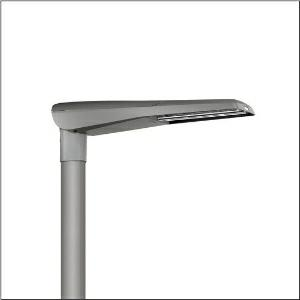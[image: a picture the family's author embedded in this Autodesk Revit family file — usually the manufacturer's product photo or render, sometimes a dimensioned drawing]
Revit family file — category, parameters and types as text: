
# Revit family: streetlight_sl_11_iq_mini___pc-l_5xc2ec1f08he_97a8
name_source: partatom
category: Lighting Fixtures
units: mm (PartAtom-declared; Revit-internal decimal feet)

## family parameters
Cut with Voids When Loaded = No
Host = Face
Light Source = No
Part Type = Normal
Room Calculation Point = No
Round Connector Dimension = Use Diameter
Shared = No

## types (1)
- --- (1 x LED, 5820 lm, 63.6 W, 2200K)
    Apparent Load = 64 VA
    CIE Flux Codes = 37 73 96 100 100
    Color Rendering = 70
    Color Temperature = 2200K
    Default Elevation = 1800 mm
    Description = Streetlight SL 11 iQ mini, mast luminaire, primary light control with 3 zone facetted reflector, of plastic, silver coated, highly specular, primary optical cover: cover, of PMMA, transparent, light distribution: PC-L, light emission: direct distribution, primary light characteristic: asymmetric, left, installation type: post-top, side-entry, lamps: LED, High Power LED, rated values: 7.110lm | 62,2W | 114,3lm/W (begin service life); end service life: 7.110lm | 65,6W; at 50% lumin. flux: 3.555lm | 29,4W | 120,9lm/W, colour temperature: 2200/2700/3000/4000K, colour rendering: CRI > 70, light colour: 722/727/730/740, light setting 1 begin service life: 100% | 7.110lm | 62,2W | 114,3lm/W | 3.000K, light setting 1 end service life: 65,6W, further light settings possible, control: Street-Remote, Auto-Match, Temp-Guard, Lumen-Switch, Night-Set, Smart-Wire, Light-Fading, Desk-Remote (wireless, voltage-free reading and setting of iQ features in the workshop via application-optimized NFC function/RFID function), optimised constant luminous flux control (CLO 2.0), with cable H07RN-F 5x 1.5mm², mains connection: 230..240V, AC, 50/60Hz, connection cable pre-assembled, cable length: 8,5m, luminaire housing, of diecast aluminium, powder-coated, Siteco® metallic grey (DB 702S), please order mast flange separately, inclination adjustable without tools: 0°, 5°, 10°, 15° (post-top) | 0°, -5°, -10°, -15° (side-entry), sealing non-destructively replaceable, multi-level sealing system, length: 736mm, width: 174mm, height: 116mm, mast flange for spigot size: 42mm (side-entry): 5XC10008XM4, 60/48mm (side-entry/post-top): 5XC10108XM2, 76/60mm (side-entry/post-top): 5XC10108XM1, equipment: Power, protection rating (complete): IP66, insulation class (complete): insulation class II (safety insulation), certification: CE, ENEC, ENEC+, VDE, impact resistance: IK10, permissible operating ambient temperature for outdoor applications: -25..+50°C, standard-compliant lighting for roads and squares, Environmental Product Declaration (EPD) tested and certified by an independent institute, packaging unit: 1 piece

Light Distribution: PC-L
    Height = 116 mm
    Lamp = 1 x LED
    Lamp Light Flux = 5820 lm
    Lamp Power = 63.6 W
    Lamp count = 1
    Length = 736 mm
    Luminous efficacy = 92 lm/W
    Manufacturer = Siteco
    ModVariant = No
    Model = 5XC2EC1F08HE
    Number of Poles = 1
    OnlyDefault = Yes
    Power Factor = 1
    Product Name = Streetlight SL 11 iQ mini | PC-L
    Product group = mast luminaire | pylon top
    ProductGroupID = 6100
    Protection Class = Protection class II
    Protection Degree = IP 66
    RLX_Detail_Level = 1
    RLX_Emergency_Light_Flux = 0 lm
    RLX_Emergency_Type = 0
    RLX_Emergency_Type_DB = No
    RlxData = <blob elided: 57449 chars, md5=d52ef5b4>
    Socket = socket
    Standby Power = 0 W
    System Light Flux = 5820 lm
    System Power = 64 W
    Type Comments = individual setting: luminous flux: 100 % | dim-lin: 254 | 866 mA
    Type Image = l_1003508.jpg
    URL = http://relux.com
    VarID = @adj_032378
    Voltage = 0 V
    Weight = 0.00 kg
    Width = 174 mm

## geometry (parser evidence)
native form markers: Blend x4, Sweep x11
no freeform markers — native parametric forms only
